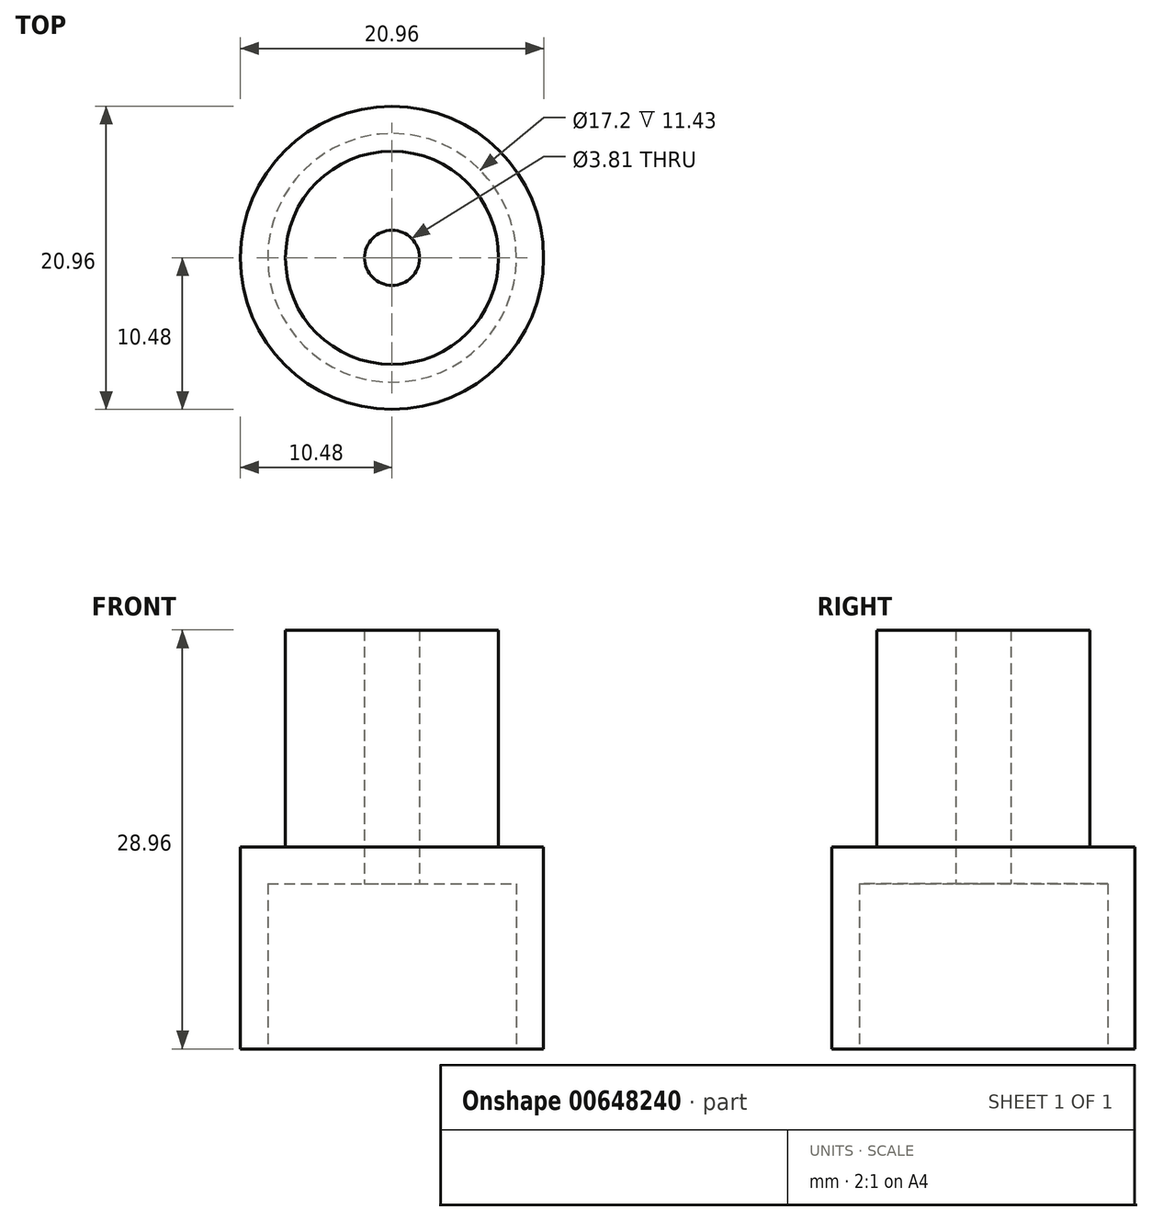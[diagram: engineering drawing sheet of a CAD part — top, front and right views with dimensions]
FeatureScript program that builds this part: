
annotation { "Feature Type Name" : "Feature", "Feature Type Description" : "" }
export const myFeature = defineFeature(function(context is Context, id is Id, definition is map)
    precondition{}
    {
        {
            var Q0;
            Q0=qCreatedBy(makeId("Top.planeOp"),FACE);
            var sketch = newSketch(context, id + "F0", { "sketchPlane" : qUnion([Q0])});
            skCircle(sketch, "E0", {"center": v(0, 0) * mm, "radius": 10.48 * mm});
            skSolve(sketch);
        }
        {
            var Q0;
            Q0 = qSketchRegion(id + "F0", true);
            var Q1;
            Q1=makeQuery(id+"F0.imprint","IMPRINT",FACE,{"disambiguationData":[TD([[makeQuery(id+"F0.imprint","IMPRINT",EDGE,{"derivedFrom":sQuery(id+"F0.wireOp",EDGE,"E0")}),1.0]])]});
            extrude(context, id + "F1", {"entities" : qUnion([Q0, Q1]), "depth" : 13.97 * mm, "offsetDistance" : 25.4 * mm});
        }
        {
            var Q0;
            Q0=makeQuery(id+"F1.opExtrude","CAP_FACE",FACE,{"disambiguationData":[OSD([sQuery(id+"F0.wireOp",EDGE,"E0")])],"isStart":false});
            var sketch = newSketch(context, id + "F2", { "sketchPlane" : qUnion([Q0])});
            skCircle(sketch, "E1", {"center": v(0, 0) * mm, "radius": 7.37 * mm});
            skSolve(sketch);
        }
        {
            var Q0;
            Q0 = qSketchRegion(id + "F2", true);
            extrude(context, id + "F3", {"entities" : qUnion([Q0]), "operationType" : NewBodyOperationType.ADD, "depth" : 15 * mm, "offsetDistance" : 25.4 * mm});
        }
        {
            var Q0;
            Q0=makeQuery(id+"F1.opExtrude","CAP_FACE",FACE,{"disambiguationData":[OSD([sQuery(id+"F0.wireOp",EDGE,"E0")])],"isStart":true});
            var sketch = newSketch(context, id + "F4", { "sketchPlane" : qUnion([Q0])});
            skCircle(sketch, "E2", {"center": v(0, 0) * mm, "radius": 8.6 * mm});
            skSolve(sketch);
        }
        {
            var Q0;
            Q0=makeQuery(id+"F4.imprint","IMPRINT",FACE,{"disambiguationData":[TD([[makeQuery(id+"F4.imprint","IMPRINT",EDGE,{"derivedFrom":sQuery(id+"F4.wireOp",EDGE,"E2")}),1.0]])]});
            extrude(context, id + "F5", {"entities" : qUnion([Q0]), "operationType" : NewBodyOperationType.REMOVE, "oppositeDirection" : true, "depth" : 11.43 * mm, "offsetDistance" : 25.4 * mm});
        }
        {
            var Q0;
            Q0=makeQuery(id+"F5.boolean.opBoolean","COPY",FACE,{"derivedFrom":makeQuery(id+"F5.opExtrude","CAP_FACE",FACE,{"disambiguationData":[OSD([sQuery(id+"F4.wireOp",EDGE,"E2")])],"isStart":false})});
            var sketch = newSketch(context, id + "F6", { "sketchPlane" : qUnion([Q0])});
            skCircle(sketch, "E3", {"center": v(0, 0) * mm, "radius": 1.9 * mm});
            skSolve(sketch);
        }
        {
            var Q0;
            Q0 = qSketchRegion(id + "F6", true);
            extrude(context, id + "F7", {"entities" : qUnion([Q0]), "operationType" : NewBodyOperationType.REMOVE, "oppositeDirection" : true, "depth" : 17.78 * mm, "offsetDistance" : 25.4 * mm});
        }
    });
